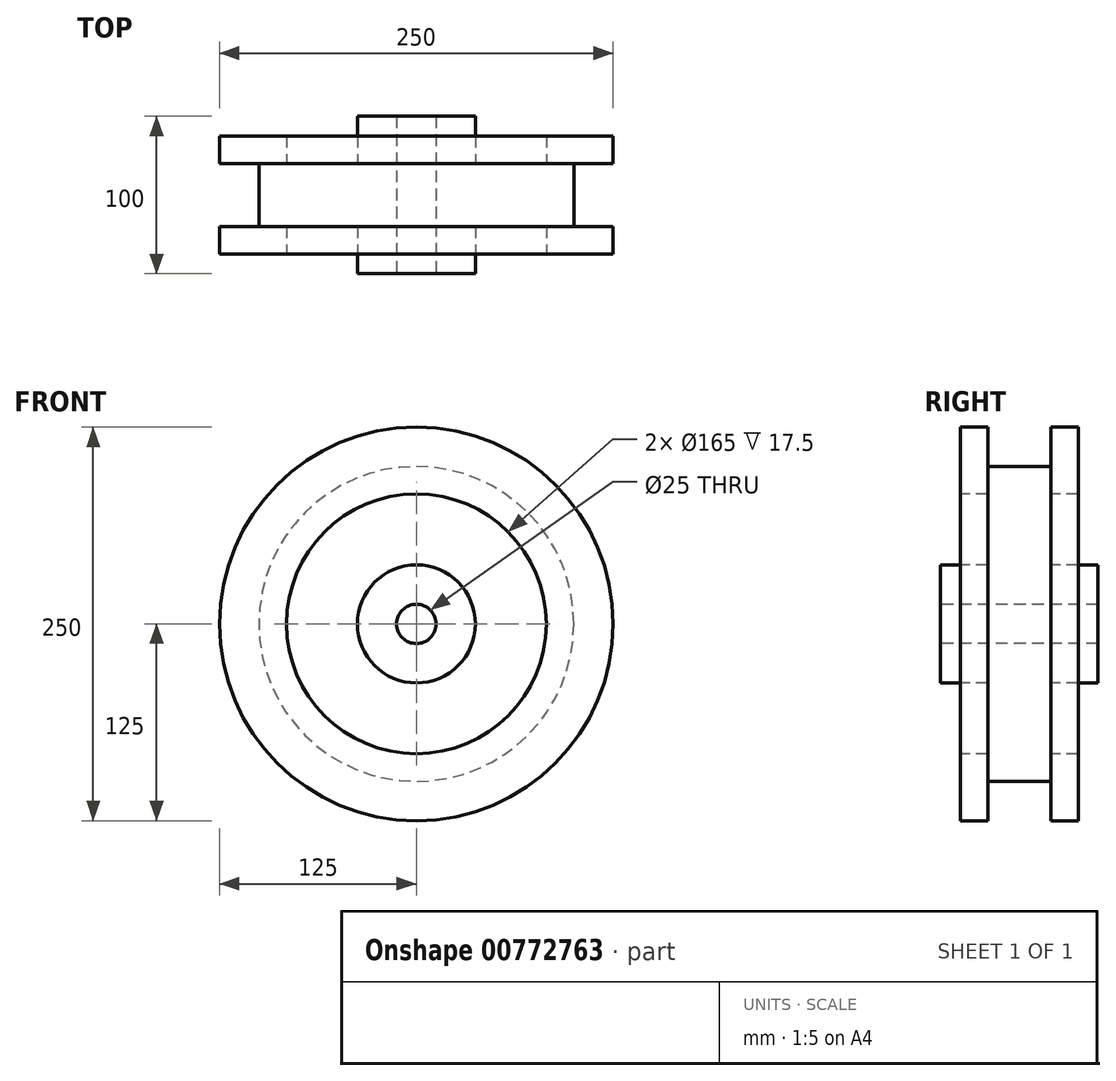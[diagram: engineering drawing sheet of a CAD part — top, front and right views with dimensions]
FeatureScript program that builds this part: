
annotation { "Feature Type Name" : "Feature", "Feature Type Description" : "" }
export const myFeature = defineFeature(function(context is Context, id is Id, definition is map)
    precondition{}
    {
        {
            var Q0;
            Q0=qCreatedBy(makeId("Right.planeOp"),FACE);
            var sketch = newSketch(context, id + "F0", { "sketchPlane" : qUnion([Q0])});
            skLineSegment(sketch, "E0", {"start": v(0, 0) * mm, "end": v(0, 106.3) * mm, "construction": true});
            skLineSegment(sketch, "E1", {"start": v(-124.14, 0) * mm, "end": v(117.2, 0) * mm, "construction": true});
            skLineSegment(sketch, "E2", {"start": v(0, 100) * mm, "end": v(-20, 100) * mm});
            skLineSegment(sketch, "E3", {"start": v(-20, 100) * mm, "end": v(-20, 125) * mm});
            skLineSegment(sketch, "E4", {"start": v(-20, 125) * mm, "end": v(-37.5, 125) * mm});
            skLineSegment(sketch, "E5", {"start": v(-37.5, 125) * mm, "end": v(-37.5, 82.5) * mm});
            skLineSegment(sketch, "E6", {"start": v(-37.5, 82.5) * mm, "end": v(-20, 82.5) * mm});
            skLineSegment(sketch, "E7", {"start": v(-20, 82.5) * mm, "end": v(-20, 37.5) * mm});
            skLineSegment(sketch, "E8", {"start": v(-20, 37.5) * mm, "end": v(-50, 37.5) * mm});
            skLineSegment(sketch, "E9", {"start": v(-50, 37.5) * mm, "end": v(-50, 12.5) * mm});
            skLineSegment(sketch, "E10", {"start": v(-50, 12.5) * mm, "end": v(0, 12.5) * mm});
            skLineSegment(sketch, "E11.MirrorCS", {"start": v(0, 100) * mm, "end": v(20, 100) * mm});
            skLineSegment(sketch, "E12.MirrorCS", {"start": v(20, 100) * mm, "end": v(20, 125) * mm});
            skLineSegment(sketch, "E13.MirrorCS", {"start": v(20, 125) * mm, "end": v(37.5, 125) * mm});
            skLineSegment(sketch, "E14.MirrorCS", {"start": v(37.5, 125) * mm, "end": v(37.5, 82.5) * mm});
            skLineSegment(sketch, "E15.MirrorCS", {"start": v(37.5, 82.5) * mm, "end": v(20, 82.5) * mm});
            skLineSegment(sketch, "E16.MirrorCS", {"start": v(20, 82.5) * mm, "end": v(20, 37.5) * mm});
            skLineSegment(sketch, "E17.MirrorCS", {"start": v(20, 37.5) * mm, "end": v(50, 37.5) * mm});
            skLineSegment(sketch, "E18.MirrorCS", {"start": v(50, 37.5) * mm, "end": v(50, 12.5) * mm});
            skLineSegment(sketch, "E19.MirrorCS", {"start": v(50, 12.5) * mm, "end": v(0, 12.5) * mm});
            skSolve(sketch);
        }
        {
            var Q0;
            Q0=makeQuery(id+"F0.imprint","IMPRINT",FACE,{"disambiguationData":[TD([[makeQuery(id+"F0.imprint","IMPRINT",EDGE,{"derivedFrom":sQuery(id+"F0.wireOp",EDGE,"E2")}),1.0]])]});
            var Q1;
            Q1=sQuery(id+"F0.wireOp",EDGE,"E1");
            revolve(context, id + "F1", {"surfaceOperationType" : NewSurfaceOperationType.NEW, "entities" : qUnion([Q0]), "axis" : qUnion([Q1]), "revolveType" : RevolveType.FULL});
        }
    });
